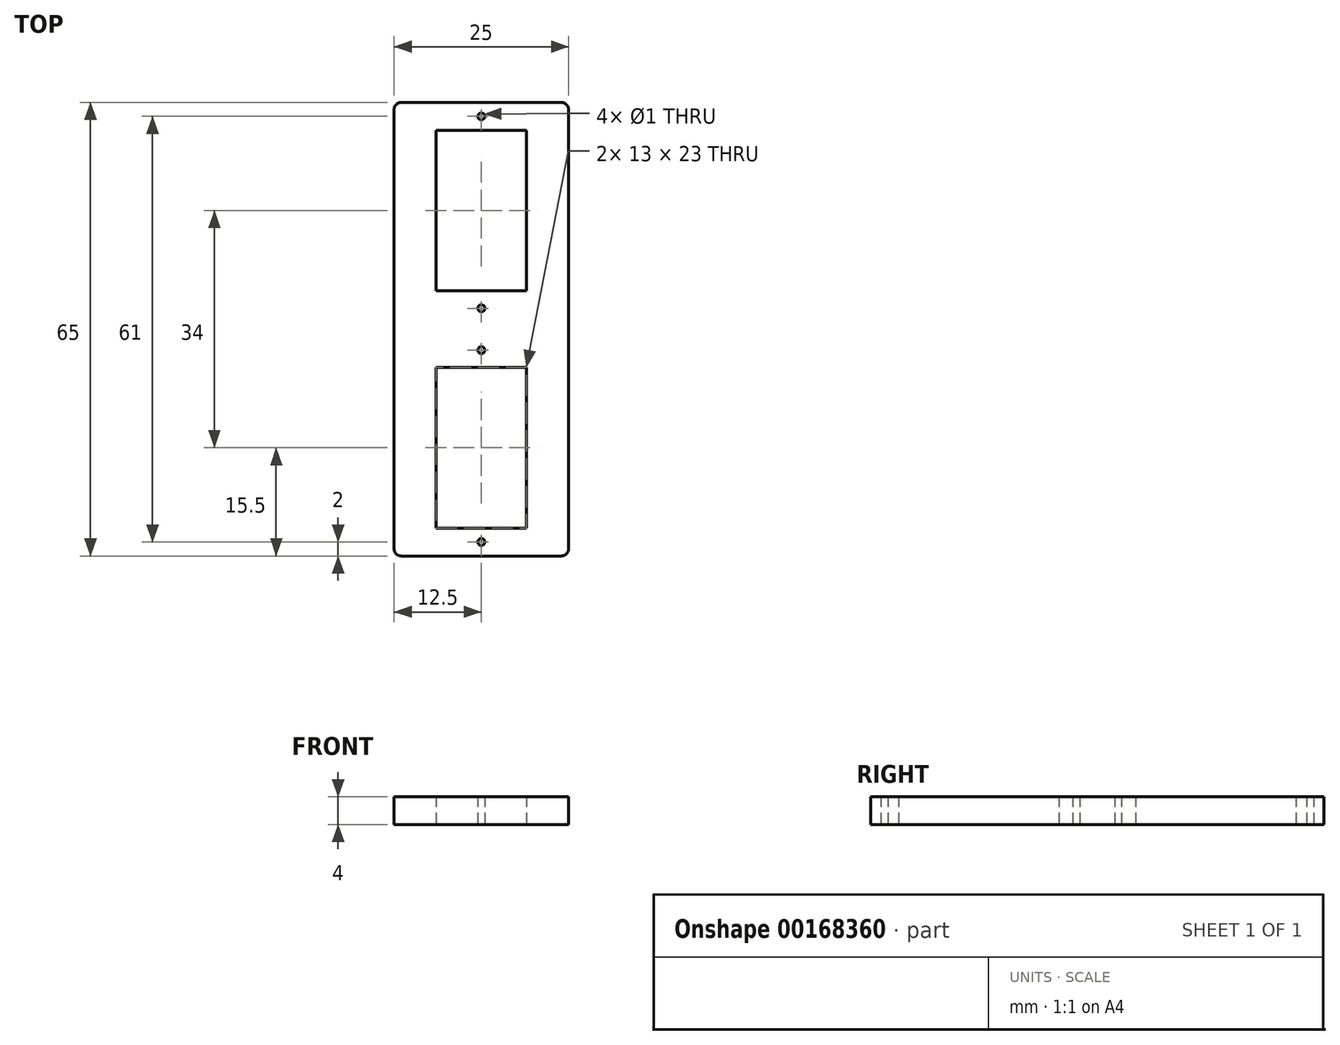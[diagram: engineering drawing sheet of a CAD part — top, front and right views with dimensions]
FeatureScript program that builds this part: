
annotation { "Feature Type Name" : "Feature", "Feature Type Description" : "" }
export const myFeature = defineFeature(function(context is Context, id is Id, definition is map)
    precondition{}
    {
        {
            var Q0;
            Q0=qCreatedBy(makeId("Top.planeOp"),FACE);
            var sketch = newSketch(context, id + "F0", { "sketchPlane" : qUnion([Q0])});
            skLineSegment(sketch, "E0.bottom", {"start": v(12.5, -32.5) * mm, "end": v(-12.5, -32.5) * mm});
            skLineSegment(sketch, "E0.top", {"start": v(12.5, 32.5) * mm, "end": v(-12.5, 32.5) * mm});
            skLineSegment(sketch, "E0.left", {"start": v(12.5, -32.5) * mm, "end": v(12.5, 32.5) * mm});
            skLineSegment(sketch, "E0.right", {"start": v(-12.5, -32.5) * mm, "end": v(-12.5, 32.5) * mm});
            skPoint(sketch, "E0.middle", {"position": v(0, 0) * mm});
            skLineSegment(sketch, "E1.bottom", {"start": v(-6.5, 28.5) * mm, "end": v(6.5, 28.5) * mm});
            skLineSegment(sketch, "E1.top", {"start": v(-6.5, 5.5) * mm, "end": v(6.5, 5.5) * mm});
            skLineSegment(sketch, "E1.left", {"start": v(-6.5, 28.5) * mm, "end": v(-6.5, 5.5) * mm});
            skLineSegment(sketch, "E1.right", {"start": v(6.5, 28.5) * mm, "end": v(6.5, 5.5) * mm});
            skPoint(sketch, "E1.middle", {"position": v(0, 17) * mm});
            skLineSegment(sketch, "E2.MirrorCS", {"start": v(-6.5, -28.5) * mm, "end": v(-6.5, -5.5) * mm});
            skLineSegment(sketch, "E3.MirrorCS", {"start": v(-6.5, -28.5) * mm, "end": v(6.5, -28.5) * mm});
            skLineSegment(sketch, "E4.MirrorCS", {"start": v(6.5, -28.5) * mm, "end": v(6.5, -5.5) * mm});
            skLineSegment(sketch, "E5.MirrorCS", {"start": v(-6.5, -5.5) * mm, "end": v(6.5, -5.5) * mm});
            skPoint(sketch, "E6", {"position": v(0, 3) * mm});
            skPoint(sketch, "E7.MirrorP", {"position": v(0, -3) * mm});
            skPoint(sketch, "E8", {"position": v(0, -30.5) * mm});
            skPoint(sketch, "E9.MirrorP", {"position": v(0, 30.5) * mm});
            skSolve(sketch);
        }
        {
            var Q0;
            Q0=makeQuery(id+"F0.imprint","IMPRINT",FACE,{"disambiguationData":[TD([[makeQuery(id+"F0.imprint","IMPRINT",EDGE,{"derivedFrom":sQuery(id+"F0.wireOp",EDGE,"E0.bottom")}),-1.0]])]});
            extrude(context, id + "F1", {"entities" : qUnion([Q0]), "depth" : 4 * mm});
        }
        {
            var Q0;
            Q0=qCreatedBy(makeId("Top.planeOp"),FACE);
            var sketch = newSketch(context, id + "F2", { "sketchPlane" : qUnion([Q0])});
            skPoint(sketch, "E10", {"position": v(0, 30.5) * mm});
            skPoint(sketch, "E11.MirrorP", {"position": v(0, -30.5) * mm});
            skSolve(sketch);
        }
        {
            var Q0;
            Q0=qCreatedBy(makeId("Top.planeOp"),FACE);
            var sketch = newSketch(context, id + "F3", { "sketchPlane" : qUnion([Q0])});
            skPoint(sketch, "E12", {"position": v(0, 3) * mm});
            skPoint(sketch, "E13.MirrorP", {"position": v(0, -3) * mm});
            skSolve(sketch);
        }
        {
            var Q0;
            Q0=sQuery(id+"F2.wireOp",VERTEX,"E10");
            var Q1;
            Q1=sQuery(id+"F3.wireOp",VERTEX,"E12");
            var Q2;
            Q2=sQuery(id+"F3.wireOp",VERTEX,"E13.MirrorP");
            var Q3;
            Q3=sQuery(id+"F2.wireOp",VERTEX,"E11.MirrorP");
            var Q4;
            Q4=makeQuery(id+"F1.opExtrude","SWEPT_BODY",BODY,{"disambiguationData":[OSD([sQuery(id+"F0.wireOp",EDGE,"E0.bottom"),sQuery(id+"F0.wireOp",EDGE,"E0.top"),sQuery(id+"F0.wireOp",EDGE,"E0.left"),sQuery(id+"F0.wireOp",EDGE,"E0.right"),sQuery(id+"F0.wireOp",EDGE,"E1.bottom"),sQuery(id+"F0.wireOp",EDGE,"E1.top"),sQuery(id+"F0.wireOp",EDGE,"E1.left"),sQuery(id+"F0.wireOp",EDGE,"E1.right"),sQuery(id+"F0.wireOp",EDGE,"E2.MirrorCS"),sQuery(id+"F0.wireOp",EDGE,"E4.MirrorCS"),sQuery(id+"F0.wireOp",EDGE,"E3.MirrorCS"),sQuery(id+"F0.wireOp",EDGE,"E5.MirrorCS")])]});
            hole(context, id + "F4", {"style" : HoleStyle.SIMPLE, "endStyle" : HoleEndStyle.THROUGH, "oppositeDirection" : true, "holeDiameter" : 1 * mm, "locations" : qUnion([Q0, Q1, Q2, Q3]), "scope" : qUnion([Q4]), "isTappedThrough" : true});
        }
        {
            var Q0;
            Q0=makeQuery(id+"F1.opExtrude","SWEPT_EDGE",EDGE,{"disambiguationData":[OSD([sQuery(id+"F0.wireOp",EDGE,"E0.top"),sQuery(id+"F0.wireOp",EDGE,"E0.right")])]});
            var Q1;
            Q1=makeQuery(id+"F1.opExtrude","SWEPT_EDGE",EDGE,{"disambiguationData":[OSD([sQuery(id+"F0.wireOp",EDGE,"E0.top"),sQuery(id+"F0.wireOp",EDGE,"E0.left")])]});
            var Q2;
            Q2=makeQuery(id+"F1.opExtrude","SWEPT_EDGE",EDGE,{"disambiguationData":[OSD([sQuery(id+"F0.wireOp",EDGE,"E0.bottom"),sQuery(id+"F0.wireOp",EDGE,"E0.right")])]});
            var Q3;
            Q3=makeQuery(id+"F1.opExtrude","SWEPT_EDGE",EDGE,{"disambiguationData":[OSD([sQuery(id+"F0.wireOp",EDGE,"E0.bottom"),sQuery(id+"F0.wireOp",EDGE,"E0.left")])]});
            fillet(context, id + "F5", {"entities" : qUnion([Q0, Q1, Q2, Q3]), "radius" : 1 * mm, "tangentPropagation" : true, "allowEdgeOverflow" : false});
        }
    });
